annotation { "Feature Type Name" : "Feature", "Feature Type Description" : "" }
export const myFeature = defineFeature(function(context is Context, id is Id, definition is map)
    precondition{}
    {
        {
            var Q0;
            Q0=qCreatedBy(makeId("Front.planeOp"),FACE);
            var sketch = newSketch(context, id + "F0", { "sketchPlane" : qUnion([Q0])});
            skCircle(sketch, "E0", {"center": v(0, 0) * mm, "radius": 10.16 * mm});
            skArc(sketch, "E1", {"start": v(-12.43, 0) * mm, "mid": v(11.73, -4.7) * mm, "end": v(-8.65, 9.1) * mm});
            skLineSegment(sketch, "E2", {"start": v(-12.43, 0) * mm, "end": v(-8.65, 9.1) * mm});
            skSolve(sketch);
        }
        {
            var Q0;
            Q0=makeQuery(id+"F0.imprint","IMPRINT",FACE,{"disambiguationData":[TD([[makeQuery(id+"F0.imprint","IMPRINT",EDGE,{"derivedFrom":sQuery(id+"F0.wireOp",EDGE,"E0")}),-1.0]])]});
            var Q1;
            Q1=sQuery(id+"F0.wireOp",EDGE,"E1");
            extrude(context, id + "F1", {"entities" : qUnion([Q0]), "surfaceEntities" : qUnion([Q1]), "depth" : 10.16 * mm});
        }
        {
            var Q0;
            Q0=makeQuery(id+"F1.opExtrude","CAP_EDGE",EDGE,{"disambiguationData":[OSD([sQuery(id+"F0.wireOp",EDGE,"E0")])],"isStart":true});
            fillet(context, id + "F2", {"entities" : qUnion([Q0]), "radius" : 1.27 * mm, "tangentPropagation" : true, "allowEdgeOverflow" : false});
        }
        {
            var Q0;
            Q0=makeQuery(id+"F1.opExtrude","CAP_EDGE",EDGE,{"disambiguationData":[OSD([sQuery(id+"F0.wireOp",EDGE,"E0")])],"isStart":false});
            fillet(context, id + "F3", {"entities" : qUnion([Q0]), "radius" : 1.27 * mm, "tangentPropagation" : true, "allowEdgeOverflow" : false});
        }
        {
            var Q0;
            Q0=makeQuery(id+"F1.opExtrude","SWEPT_FACE",FACE,{"disambiguationData":[OSD([sQuery(id+"F0.wireOp",EDGE,"E2")])]});
            cPlane(context, id + "F4", {"entities" : qUnion([Q0]), "cplaneType" : CPlaneType.OFFSET, "offset" : 0 * mm, "width" : 152.4 * mm, "height" : 152.4 * mm});
        }
        {
            var Q0;
            Q0=qCreatedBy(id+"F4.planeOp",FACE);
            var sketch = newSketch(context, id + "F5", { "sketchPlane" : qUnion([Q0])});
            skPoint(sketch, "E3.middle", {"position": v(5.24, 0) * mm});
            skLineSegment(sketch, "E4.bottom", {"start": v(-32.16, 15.5) * mm, "end": v(42.63, 15.5) * mm});
            skLineSegment(sketch, "E4.top", {"start": v(-32.16, -15.5) * mm, "end": v(42.63, -15.5) * mm});
            skLineSegment(sketch, "E4.left", {"start": v(-32.16, 15.5) * mm, "end": v(-32.16, -15.5) * mm});
            skLineSegment(sketch, "E4.right", {"start": v(42.63, 15.5) * mm, "end": v(42.63, -15.5) * mm});
            skSolve(sketch);
        }
        {
            var Q0;
            Q0=makeQuery(id+"F5.imprint","IMPRINT",FACE,{"disambiguationData":[TD([[makeQuery(id+"F5.imprint","IMPRINT",EDGE,{"derivedFrom":sQuery(id+"F5.wireOp",EDGE,"E4.bottom")}),-1.0]])]});
            extrude(context, id + "F6", {"entities" : qUnion([Q0]), "operationType" : NewBodyOperationType.ADD, "depth" : 5.84 * mm, "offsetDistance" : 25.4 * mm});
        }
        {
            var Q0;
            Q0=makeQuery(id+"F6.opExtrude","CAP_FACE",FACE,{"disambiguationData":[OSD([sQuery(id+"F5.wireOp",EDGE,"E4.bottom"),sQuery(id+"F5.wireOp",EDGE,"E4.top"),sQuery(id+"F5.wireOp",EDGE,"E4.left"),sQuery(id+"F5.wireOp",EDGE,"E4.right")])],"isStart":false});
            var sketch = newSketch(context, id + "F7", { "sketchPlane" : qUnion([Q0])});
            skText(sketch, "E5", { "text": "Silhouette Ballroom Studios", "fontName": "OpenSans-Regular.ttf"});
            skText(sketch, "E6", { "text": "Tango", "fontName": "OpenSans-Regular.ttf"});
            skText(sketch, "E7", { "text": "Rumba", "fontName": "OpenSans-Regular.ttf"});
            skText(sketch, "E8", { "text": "West Coast Swing", "fontName": "OpenSans-Regular.ttf"});
            skText(sketch, "E9", { "text": "Viennese Waltz", "fontName": "OpenSans-Regular.ttf"});
            skText(sketch, "E10", { "text": "Polka", "fontName": "OpenSans-Regular.ttf"});
            skText(sketch, "E11", { "text": "Foxtrot", "fontName": "OpenSans-Regular.ttf"});
            skText(sketch, "E12", { "text": "Samba", "fontName": "OpenSans-Regular.ttf"});
            const initialGuessF7  = {"E5": [-0.02231, 0.00882, 1, 0, 0.00317], "E6": [-0.02792, 0.00238, 1, 0, 0.00317], "E7": [-0.01774, -0.00266, 1, 0, 0.00315], "E8": [0.00138, 0.0024, 1, 0, 0.00312], "E9": [-0.02374, -0.00937, 1, 0, 0.00308], "E10": [0.00924, -0.00465, 1, 0, 0.0031], "E11": [0.02522, -0.0072, 1, 0, 0.00313], "E12": [0.0174, -0.01319, 1, 0, 0.00317]};
            skSetInitialGuess(sketch, initialGuessF7);
            skSolve(sketch);
        }
        {
            var Q0;
            Q0 = qSketchRegion(id + "F7", true);
            extrude(context, id + "F8", {"entities" : qUnion([Q0]), "operationType" : NewBodyOperationType.ADD, "depth" : 1.52 * mm, "offsetDistance" : 25.4 * mm});
        }
    });